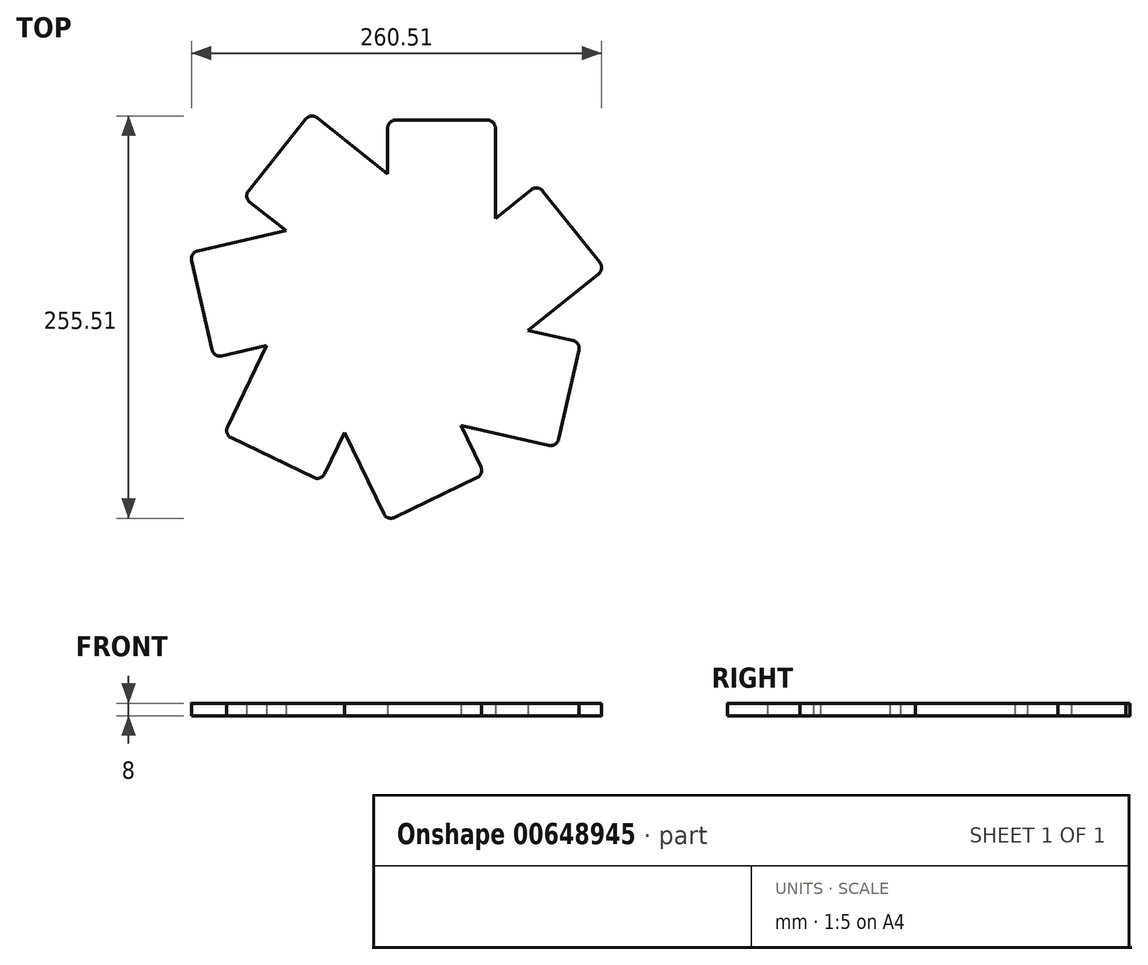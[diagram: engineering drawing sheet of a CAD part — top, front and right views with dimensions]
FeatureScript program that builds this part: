
annotation { "Feature Type Name" : "Feature", "Feature Type Description" : "" }
export const myFeature = defineFeature(function(context is Context, id is Id, definition is map)
    precondition{}
    {
        {
            var Q0;
            Q0=qCreatedBy(makeId("Top.planeOp"),FACE);
            var sketch = newSketch(context, id + "F0", { "sketchPlane" : qUnion([Q0])});
            skLineSegment(sketch, "E0.bottom", {"start": v(-24.7, 82.46) * mm, "end": v(33.7, 82.46) * mm});
            skLineSegment(sketch, "E0.top", {"start": v(-24.7, -42.01) * mm, "end": v(33.7, -42.01) * mm});
            skLineSegment(sketch, "E0.left", {"start": v(-29.7, 77.46) * mm, "end": v(-29.7, -37.01) * mm});
            skLineSegment(sketch, "E0.right", {"start": v(38.7, 77.46) * mm, "end": v(38.7, -37.01) * mm});
            skPoint(sketch, "E1.visualSharp", {"position": v(-29.7, 82.46) * mm});
            skArc(sketch, "E1.filletArc", {"start": v(-24.7, 82.46) * mm, "mid": v(-28.25, 81) * mm, "end": v(-29.7, 77.46) * mm});
            skPoint(sketch, "E2.visualSharp", {"position": v(38.7, 82.46) * mm});
            skArc(sketch, "E2.filletArc", {"start": v(38.7, 77.46) * mm, "mid": v(37.23, 81) * mm, "end": v(33.7, 82.46) * mm});
            skPoint(sketch, "E3.visualSharp", {"position": v(38.7, -42.01) * mm});
            skArc(sketch, "E3.filletArc", {"start": v(33.7, -42.01) * mm, "mid": v(37.23, -40.55) * mm, "end": v(38.7, -37.01) * mm});
            skPoint(sketch, "E4.visualSharp", {"position": v(-29.7, -42.01) * mm});
            skArc(sketch, "E4.filletArc", {"start": v(-29.7, -37.01) * mm, "mid": v(-28.25, -40.55) * mm, "end": v(-24.7, -42.01) * mm});
            skSolve(sketch);
        }
        {
            var Q0;
            Q0 = qSketchRegion(id + "F0", true);
            extrude(context, id + "F1", {"entities" : qUnion([Q0]), "depth" : 8 * mm, "offsetDistance" : 25 * mm});
        }
        {
            var Q0;
            Q0=makeQuery(id+"F1.opExtrude","SWEPT_BODY",BODY,{"disambiguationData":[OSD([sQuery(id+"F0.wireOp",EDGE,"E0.bottom"),sQuery(id+"F0.wireOp",EDGE,"E0.top"),sQuery(id+"F0.wireOp",EDGE,"E0.left"),sQuery(id+"F0.wireOp",EDGE,"E0.right"),sQuery(id+"F0.wireOp",EDGE,"E1.filletArc"),sQuery(id+"F0.wireOp",EDGE,"E2.filletArc"),sQuery(id+"F0.wireOp",EDGE,"E3.filletArc"),sQuery(id+"F0.wireOp",EDGE,"E4.filletArc")])]});
            var Q1;
            Q1=makeQuery(id+"F1.opExtrude","SWEPT_FACE",FACE,{"disambiguationData":[OSD([sQuery(id+"F0.wireOp",EDGE,"E4.filletArc")])]});
            circularPattern(context, id + "F2", {"operationType" : NewBodyOperationType.ADD, "entities" : qUnion([Q0]), "axis" : qUnion([Q1]), "angle" : 360 * degree, "instanceCount" : 7, "equalSpace" : true});
        }
    });
